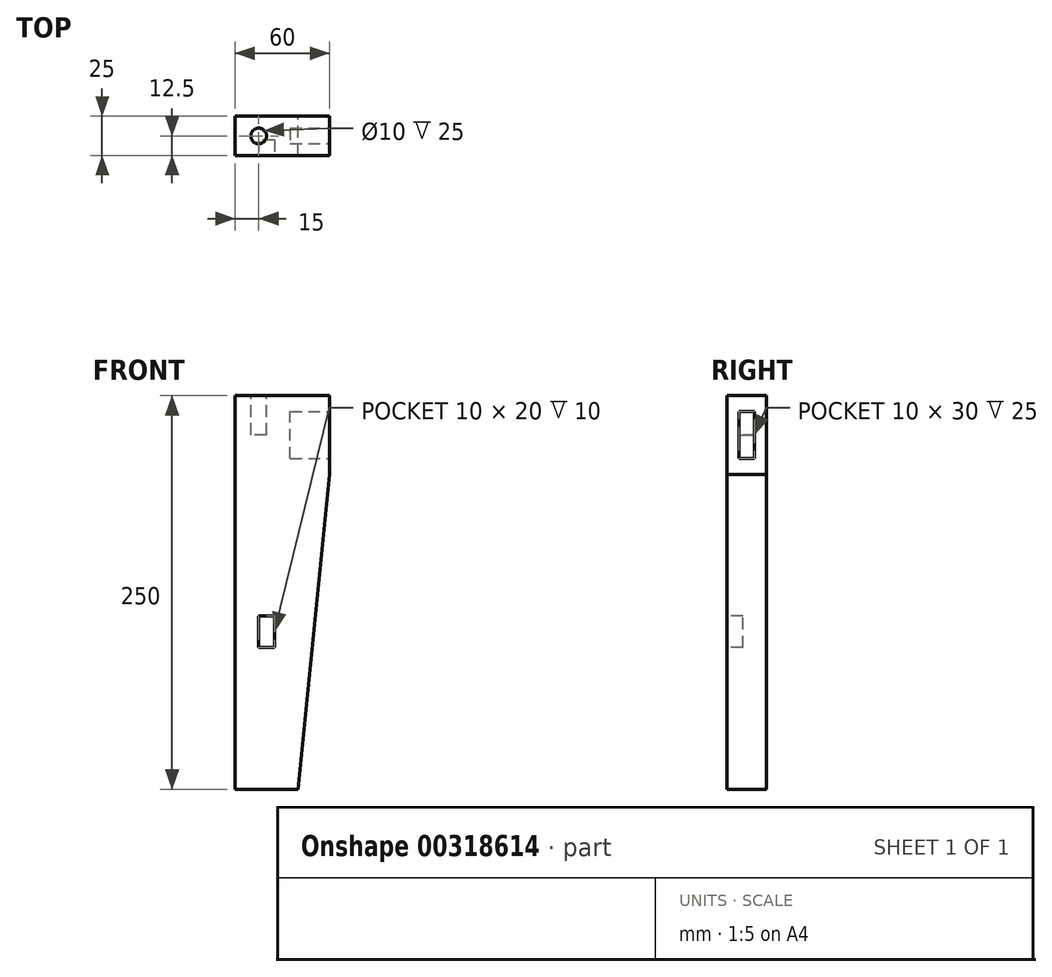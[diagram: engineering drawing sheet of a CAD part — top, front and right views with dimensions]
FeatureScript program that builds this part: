
annotation { "Feature Type Name" : "Feature", "Feature Type Description" : "" }
export const myFeature = defineFeature(function(context is Context, id is Id, definition is map)
    precondition{}
    {
        {
            var Q0;
            Q0=qCreatedBy(makeId("Front.planeOp"),FACE);
            var sketch = newSketch(context, id + "F0", { "sketchPlane" : qUnion([Q0])});
            skLineSegment(sketch, "E0", {"start": v(0, 0) * mm, "end": v(20, 200) * mm});
            skLineSegment(sketch, "E1", {"start": v(20, 200) * mm, "end": v(20, 250) * mm});
            skLineSegment(sketch, "E2", {"start": v(20, 250) * mm, "end": v(-40, 250) * mm});
            skLineSegment(sketch, "E3", {"start": v(-40, 250) * mm, "end": v(-40, 0) * mm});
            skLineSegment(sketch, "E4", {"start": v(-40, 0) * mm, "end": v(0, 0) * mm});
            skSolve(sketch);
        }
        {
            var Q0;
            Q0=qSketchRegion(id+"F0",true);
            extrude(context, id + "F1", {"entities" : qUnion([Q0]), "endBound" : BoundingType.SYMMETRIC, "depth" : 25 * mm});
        }
        {
            var Q0;
            Q0=makeQuery(id+"F1.opExtrude","SWEPT_FACE",FACE,{"disambiguationData":[OSD([sQuery(id+"F0.wireOp",EDGE,"E1")])]});
            var sketch = newSketch(context, id + "F2", { "sketchPlane" : qUnion([Q0])});
            skLineSegment(sketch, "E5", {"start": v(0, 200) * mm, "end": v(0, 250) * mm, "construction": true});
            skLineSegment(sketch, "E6.rect.bottom", {"start": v(5, 210) * mm, "end": v(-5, 210) * mm});
            skLineSegment(sketch, "E6.rect.top", {"start": v(5, 240) * mm, "end": v(-5, 240) * mm});
            skLineSegment(sketch, "E6.rect.left", {"start": v(5, 210) * mm, "end": v(5, 240) * mm});
            skLineSegment(sketch, "E6.rect.right", {"start": v(-5, 210) * mm, "end": v(-5, 240) * mm});
            skPoint(sketch, "E6.rect.middle", {"position": v(0, 225) * mm});
            skSolve(sketch);
        }
        {
            var Q0;
            Q0=qSketchRegion(id+"F2",true);
            extrude(context, id + "F3", {"entities" : qUnion([Q0]), "operationType" : NewBodyOperationType.REMOVE, "oppositeDirection" : true, "depth" : 25 * mm});
        }
        {
            var Q0;
            Q0=makeQuery(id+"F1.opExtrude","CAP_FACE",FACE,{"disambiguationData":[OSD([sQuery(id+"F0.wireOp",EDGE,"E0"),sQuery(id+"F0.wireOp",EDGE,"E1"),sQuery(id+"F0.wireOp",EDGE,"E2"),sQuery(id+"F0.wireOp",EDGE,"E3"),sQuery(id+"F0.wireOp",EDGE,"E4")])],"isStart":false});
            var sketch = newSketch(context, id + "F4", { "sketchPlane" : qUnion([Q0])});
            skLineSegment(sketch, "E7.rect.bottom", {"start": v(-15, 90) * mm, "end": v(-25, 90) * mm});
            skLineSegment(sketch, "E7.rect.top", {"start": v(-15, 110) * mm, "end": v(-25, 110) * mm});
            skLineSegment(sketch, "E7.rect.left", {"start": v(-15, 90) * mm, "end": v(-15, 110) * mm});
            skLineSegment(sketch, "E7.rect.right", {"start": v(-25, 90) * mm, "end": v(-25, 110) * mm});
            skPoint(sketch, "E7.rect.middle", {"position": v(-20, 100) * mm});
            skSolve(sketch);
        }
        {
            var Q0;
            Q0=qSketchRegion(id+"F4",true);
            extrude(context, id + "F5", {"entities" : qUnion([Q0]), "operationType" : NewBodyOperationType.REMOVE, "oppositeDirection" : true, "depth" : 10 * mm});
        }
        {
            var Q0;
            Q0=makeQuery(id+"F1.opExtrude","SWEPT_FACE",FACE,{"disambiguationData":[OSD([sQuery(id+"F0.wireOp",EDGE,"E2")])]});
            var sketch = newSketch(context, id + "F6", { "sketchPlane" : qUnion([Q0])});
            skLineSegment(sketch, "E8", {"start": v(-40, 0) * mm, "end": v(20, 0) * mm, "construction": true});
            skCircle(sketch, "E9", {"center": v(-25, 0) * mm, "radius": 5 * mm});
            skSolve(sketch);
        }
        {
            var Q0;
            Q0=qSketchRegion(id+"F6",true);
            extrude(context, id + "F7", {"entities" : qUnion([Q0]), "operationType" : NewBodyOperationType.REMOVE, "oppositeDirection" : true, "depth" : 25 * mm});
        }
    });
